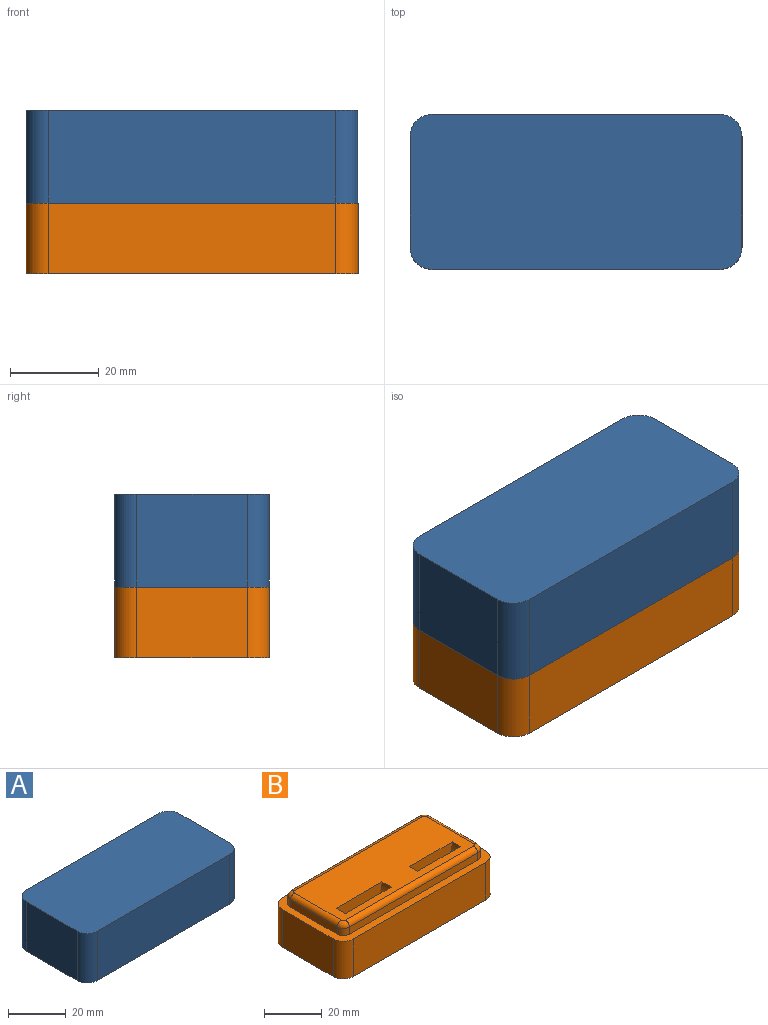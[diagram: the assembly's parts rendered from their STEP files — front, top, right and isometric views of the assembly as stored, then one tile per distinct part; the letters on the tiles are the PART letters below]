
ASSEMBLY  parts=2 mates=1
PART A: 19 faces, bbox 75x35x21 mm
  f0: plane 75x35mm, normal (0,0,-1), area 590.6mm2, adj f1,f2,f3,f4,f5,f6,f7,f8
  f1: plane 25x21mm, normal (1,0,0), area 525mm2, adj f0,f2,f8,f9
  f2: cylinder r=5mm len=21mm, axis (0,0,-1), area 164.9mm2, adj f0,f1,f3,f9
  f3: plane 65x21mm, normal (0,1,0), area 1365mm2, adj f0,f2,f4,f9
  f4: cylinder r=5mm len=21mm, axis (0,0,-1), area 164.9mm2, adj f0,f3,f5,f9
  f5: plane 25x21mm, normal (-1,0,0), area 525mm2, adj f0,f4,f6,f9
  f6: cylinder r=5mm len=21mm, axis (0,0,-1), area 164.9mm2, adj f0,f5,f7,f9
  f7: plane 65x21mm, normal (0,-1,0), area 1365mm2, adj f0,f6,f8,f9
  f8: cylinder r=5mm len=21mm, axis (0,0,-1), area 164.9mm2, adj f0,f1,f7,f9
  f9: plane 75x35mm, normal (0,0,1), area 2603.5mm2, adj f1,f2,f3,f4,f5,f6,f7,f8
  f10: plane 23.2x16mm, normal (-1,0,0), area 371.2mm2, adj f0,f11,f17,f18
  f11: cylinder r=3mm len=16mm, axis (0,0,-1), area 75.4mm2, adj f0,f10,f12,f18
  f12: plane 63.2x16mm, normal (0,1,0), area 1011.2mm2, adj f0,f11,f13,f18
  f13: cylinder r=3mm len=16mm, axis (0,0,-1), area 75.4mm2, adj f0,f12,f14,f18
  f14: plane 23.2x16mm, normal (1,0,0), area 371.2mm2, adj f0,f13,f15,f18
  f15: cylinder r=3mm len=16mm, axis (0,0,-1), area 75.4mm2, adj f0,f14,f16,f18
  f16: plane 63.2x16mm, normal (0,-1,0), area 1011.2mm2, adj f0,f15,f17,f18
  f17: cylinder r=3mm len=16mm, axis (0,0,-1), area 75.4mm2, adj f0,f10,f16,f18
  f18: plane 69.2x29.2mm, normal (0,0,-1), area 2012.9mm2, adj f10,f11,f12,f13,f14,f15,f16,f17
PART B: 33 faces, bbox 75x35x21 mm
  f0: plane 25x16mm, normal (1,0,0), area 400mm2, adj f4,f7,f8,f17
  f1: plane 65x16mm, normal (0,1,0), area 1040mm2, adj f4,f5,f8,f17
  f2: plane 25x16mm, normal (-1,0,0), area 400mm2, adj f5,f6,f8,f17
  f3: plane 65x16mm, normal (0,-1,0), area 1040mm2, adj f6,f7,f8,f17
  f4: cylinder r=5mm len=16mm, axis (0,0,-1), area 125.7mm2, adj f0,f1,f8,f17
  f5: cylinder r=5mm len=16mm, axis (0,0,-1), area 125.7mm2, adj f1,f2,f8,f17
  f6: cylinder r=5mm len=16mm, axis (0,0,-1), area 125.7mm2, adj f2,f3,f8,f17
  f7: cylinder r=5mm len=16mm, axis (0,0,-1), area 125.7mm2, adj f0,f3,f8,f17
  f8: plane 75x35mm, normal (0,0,-1), area 2603.5mm2, adj f0,f1,f2,f3,f4,f5,f6,f7
  f9: cylinder r=3mm len=3mm, axis (0,0,1), area 14.1mm2, adj f10,f16,f17,f27
  f10: plane 23x3mm, normal (1,0,0), area 69mm2, adj f9,f11,f17,f29
  f11: cylinder r=3mm len=3mm, axis (0,0,1), area 14.1mm2, adj f10,f12,f17,f31
  f12: plane 63x3mm, normal (0,-1,0), area 189mm2, adj f11,f13,f17,f32
  f13: cylinder r=3mm len=3mm, axis (0,0,1), area 14.1mm2, adj f12,f14,f17,f30
  f14: plane 23x3mm, normal (-1,0,0), area 69mm2, adj f13,f15,f17,f28
  f15: cylinder r=3mm len=3mm, axis (0,0,1), area 14.1mm2, adj f14,f16,f17,f26
  f16: plane 63x3mm, normal (0,1,0), area 189mm2, adj f9,f15,f17,f25
  f17: plane 75x35mm, normal (0,0,1), area 610.3mm2, adj f0,f1,f2,f3,f4,f5,f6,f7
  f18: plane 22.5x11.25mm, normal (0,1,0), area 198.8mm2, adj f20,f24
  f19: plane 22.5x11.25mm, normal (0,-1,0), area 198.8mm2, adj f20,f24
  f20: cylinder r=11.25mm len=22.5mm, axis (0,-1,0), area 159mm2, adj f18,f19,f24
  f21: plane 21x10.5mm, normal (0,1,0), area 173.2mm2, adj f23,f24
  f22: plane 21x10.5mm, normal (0,-1,0), area 173.2mm2, adj f23,f24
  f23: cylinder r=10.5mm len=21mm, axis (0,-1,0), area 131.9mm2, adj f21,f22,f24
  f24: plane 65x25mm, normal (0,0,1), area 1438.9mm2, adj f18,f19,f20,f21,f22,f23,f25,f26
  f25: cylinder r=2mm len=63mm, axis (-1,0,0), area 197.9mm2, adj f16,f24,f26,f27
  f26: torus R=1mm, axis (0,0,1), area 11.2mm2, adj f15,f24,f25,f28
  f27: torus R=1mm, axis (0,0,1), area 11.2mm2, adj f9,f24,f25,f29
  f28: cylinder r=2mm len=23mm, axis (0,-1,0), area 72.3mm2, adj f14,f24,f26,f30
  f29: cylinder r=2mm len=23mm, axis (0,1,0), area 72.3mm2, adj f10,f24,f27,f31
  f30: torus R=1mm, axis (0,0,1), area 11.2mm2, adj f13,f24,f28,f32
  f31: torus R=1mm, axis (0,0,1), area 11.2mm2, adj f11,f24,f29,f32
  f32: cylinder r=2mm len=63mm, axis (1,0,0), area 197.9mm2, adj f12,f24,f30,f31
PLACE A t=(-7.96,9.37,-0.68)mm
PLACE B t=(-10.47,-7,-16.68)mm
MATE fastened B.f17 <-> A.f0  axis (0,0,-1) through (-42.97,18,-0.68)mm
